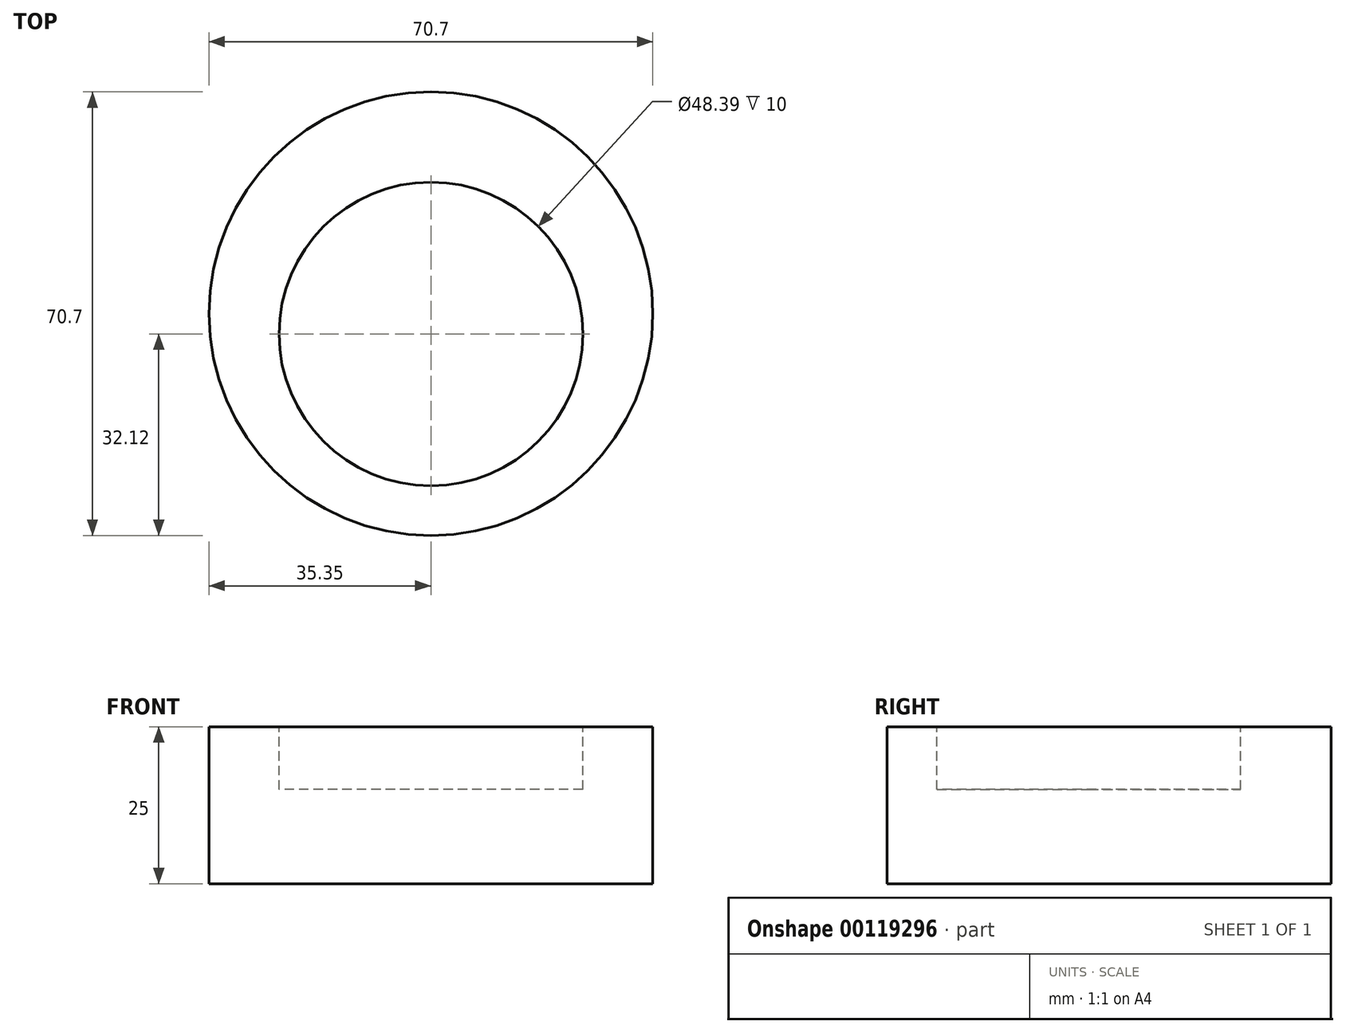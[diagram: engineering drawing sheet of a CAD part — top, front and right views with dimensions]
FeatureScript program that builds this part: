
annotation { "Feature Type Name" : "Feature", "Feature Type Description" : "" }
export const myFeature = defineFeature(function(context is Context, id is Id, definition is map)
    precondition{}
    {
        {
            var Q0;
            Q0=qCreatedBy(makeId("Top.planeOp"),FACE);
            var sketch = newSketch(context, id + "F0", { "sketchPlane" : qUnion([Q0])});
            skCircle(sketch, "E0", {"center": v(0, 3.23) * mm, "radius": 35.35 * mm});
            skSolve(sketch);
        }
        {
            var Q0;
            Q0=makeQuery(id+"F0.imprint","IMPRINT",FACE,{"disambiguationData":[TD([[makeQuery(id+"F0.imprint","IMPRINT",EDGE,{"derivedFrom":sQuery(id+"F0.wireOp",EDGE,"E0")}),1.0]])]});
            extrude(context, id + "F1", {"entities" : qUnion([Q0]), "depth" : 25 * mm});
        }
        {
            var Q0;
            Q0=makeQuery(id+"F1.opExtrude","CAP_FACE",FACE,{"disambiguationData":[OSD([sQuery(id+"F0.wireOp",EDGE,"E0")])],"isStart":false});
            var sketch = newSketch(context, id + "F2", { "sketchPlane" : qUnion([Q0])});
            skCircle(sketch, "E1", {"center": v(0, 0) * mm, "radius": 24.2 * mm});
            skSolve(sketch);
        }
        {
            var Q0;
            Q0=makeQuery(id+"F2.imprint","IMPRINT",FACE,{"disambiguationData":[TD([[makeQuery(id+"F2.imprint","IMPRINT",EDGE,{"derivedFrom":sQuery(id+"F2.wireOp",EDGE,"E1")}),1.0]])]});
            extrude(context, id + "F3", {"entities" : qUnion([Q0]), "operationType" : NewBodyOperationType.ADD, "depth" : 15 * mm});
        }
        {
            var Q0;
            Q0=makeQuery(id+"F3.opExtrude","CAP_FACE",FACE,{"disambiguationData":[OSD([sQuery(id+"F2.wireOp",EDGE,"E1")])],"isStart":false});
            extrude(context, id + "F4", {"entities" : qUnion([Q0]), "operationType" : NewBodyOperationType.REMOVE, "oppositeDirection" : true, "depth" : 25 * mm});
        }
    });
